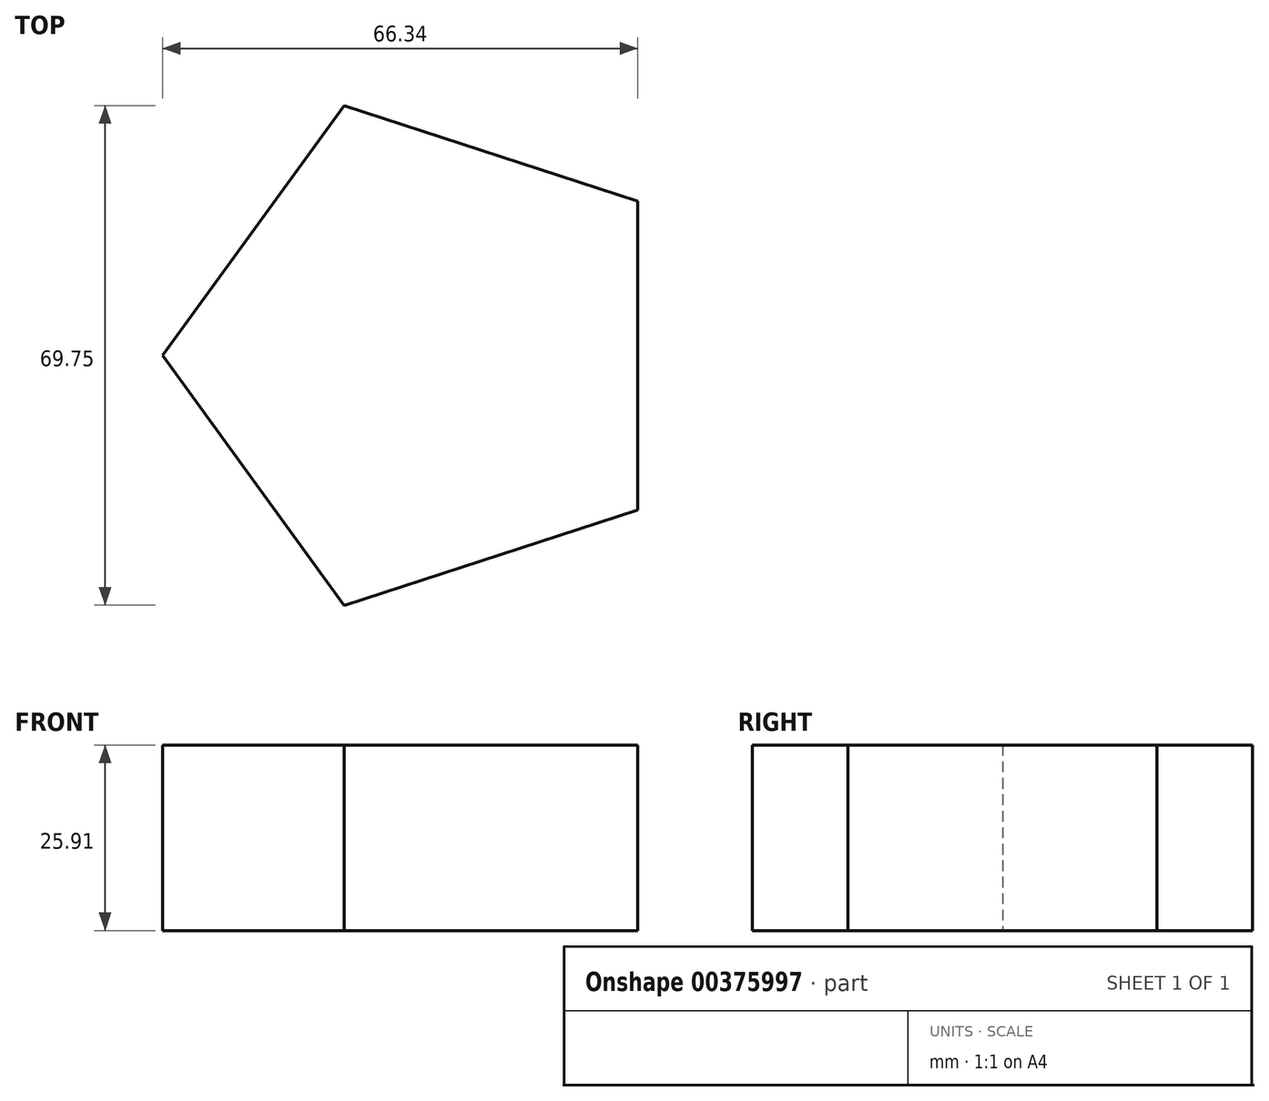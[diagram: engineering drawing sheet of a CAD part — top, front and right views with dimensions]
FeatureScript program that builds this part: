
annotation { "Feature Type Name" : "Feature", "Feature Type Description" : "" }
export const myFeature = defineFeature(function(context is Context, id is Id, definition is map)
    precondition{}
    {
        {
            var Q0;
            Q0=qCreatedBy(makeId("Top.planeOp"),FACE);
            var sketch = newSketch(context, id + "F0", { "sketchPlane" : qUnion([Q0])});
            skCircle(sketch, "E0.cCircle", {"center": v(3.26, -0.66) * mm, "radius": 29.67 * mm, "construction": true});
            skLineSegment(sketch, "E0.0", {"start": v(32.93, 20.9) * mm, "end": v(32.93, -22.21) * mm});
            skLineSegment(sketch, "E0.1", {"start": v(32.93, -22.21) * mm, "end": v(-8.07, -35.53) * mm});
            skLineSegment(sketch, "E0.2", {"start": v(-8.07, -35.53) * mm, "end": v(-33.41, -0.66) * mm});
            skLineSegment(sketch, "E0.3", {"start": v(-33.41, -0.66) * mm, "end": v(-8.07, 34.22) * mm});
            skLineSegment(sketch, "E0.4", {"start": v(-8.07, 34.22) * mm, "end": v(32.93, 20.9) * mm});
            skPoint(sketch, "E0.0.midPoint", {"position": v(32.93, -0.66) * mm});
            skSolve(sketch);
        }
        {
            var Q0;
            Q0 = qSketchRegion(id + "F0", true);
            extrude(context, id + "F1", {"entities" : qUnion([Q0]), "depth" : 25.9 * mm});
        }
    });
